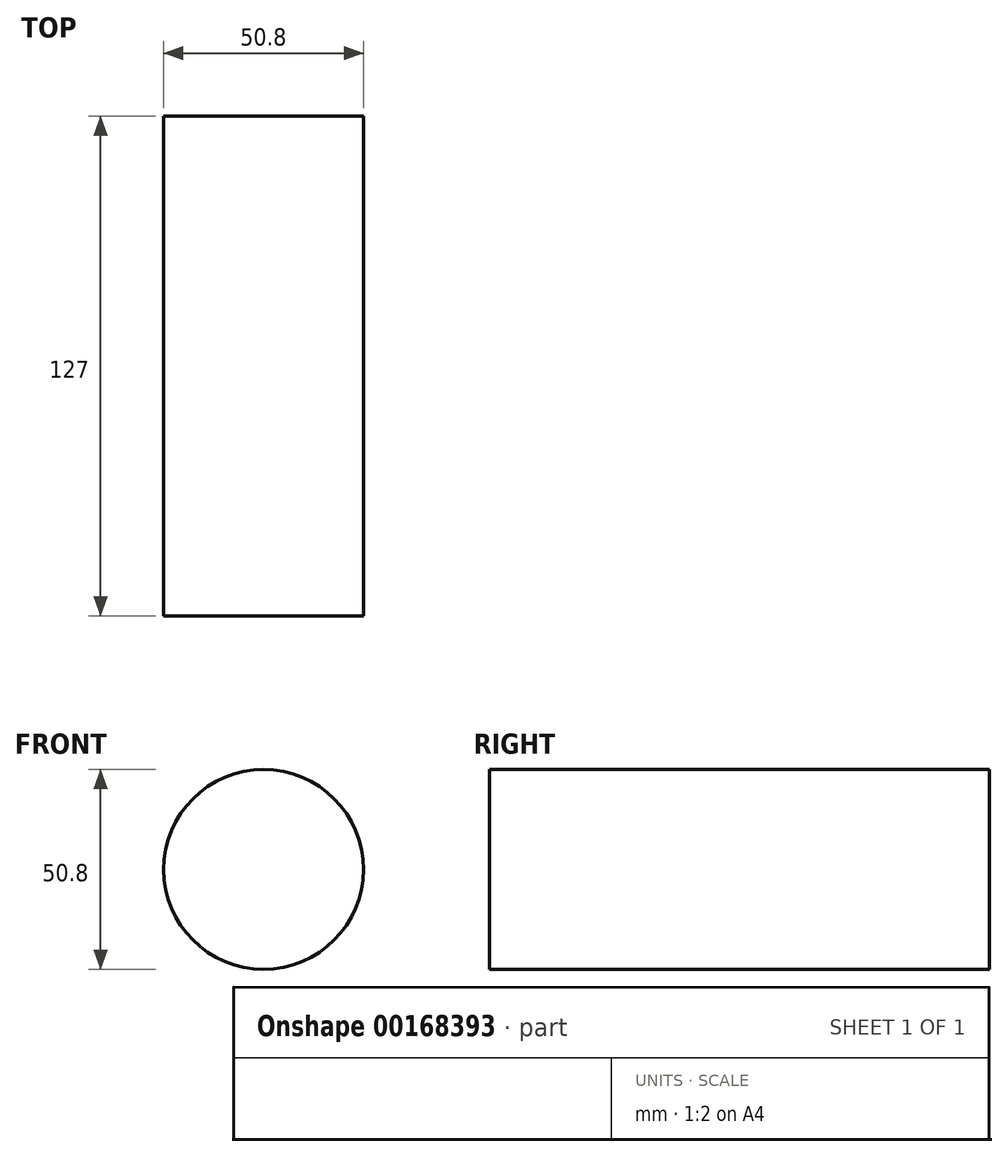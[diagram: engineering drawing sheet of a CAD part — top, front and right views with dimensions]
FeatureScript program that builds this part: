
annotation { "Feature Type Name" : "Feature", "Feature Type Description" : "" }
export const myFeature = defineFeature(function(context is Context, id is Id, definition is map)
    precondition{}
    {
        {
            var Q0;
            Q0=qCreatedBy(makeId("Front.planeOp"),FACE);
            var sketch = newSketch(context, id + "F0", { "sketchPlane" : qUnion([Q0])});
            skCircle(sketch, "E0", {"center": v(0, 0) * mm, "radius": 25.4 * mm});
            skSolve(sketch);
        }
        {
            var Q0;
            Q0=makeQuery(id+"F0.imprint","IMPRINT",FACE,{"disambiguationData":[TD([[makeQuery(id+"F0.imprint","IMPRINT",EDGE,{"derivedFrom":sQuery(id+"F0.wireOp",EDGE,"E0")}),1.0]])]});
            extrude(context, id + "F1", {"entities" : qUnion([Q0]), "depth" : 127 * mm});
        }
    });
